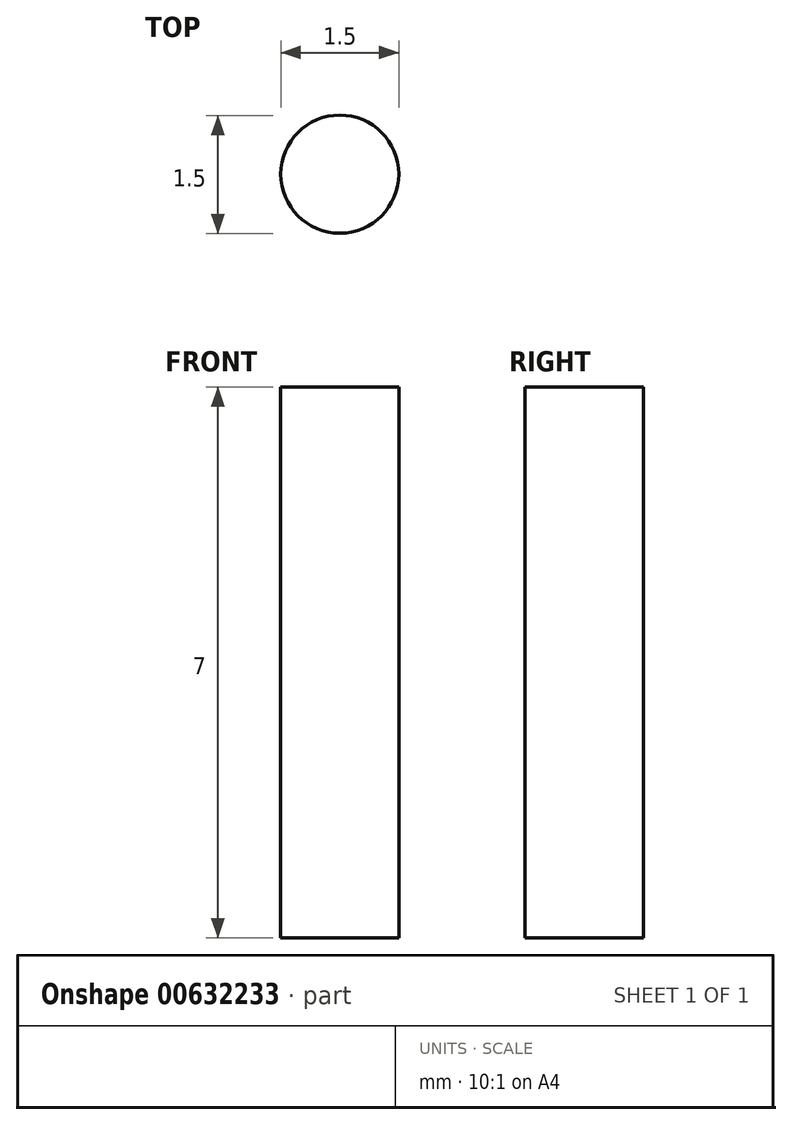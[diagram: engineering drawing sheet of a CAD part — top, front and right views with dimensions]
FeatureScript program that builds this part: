
annotation { "Feature Type Name" : "Feature", "Feature Type Description" : "" }
export const myFeature = defineFeature(function(context is Context, id is Id, definition is map)
    precondition{}
    {
        {
            var Q0;
            Q0=qCreatedBy(makeId("Top.planeOp"),FACE);
            var sketch = newSketch(context, id + "F0", { "sketchPlane" : qUnion([Q0])});
            skCircle(sketch, "E0", {"center": v(-13.28, 7.7) * mm, "radius": 0.75 * mm});
            skCircle(sketch, "E1", {"center": v(-7.79, 7.36) * mm, "radius": 1 * mm});
            skLineSegment(sketch, "E2.bottom", {"start": v(-10.46, 9.93) * mm, "end": v(-4.85, 9.93) * mm});
            skLineSegment(sketch, "E2.top", {"start": v(-10.46, 4.96) * mm, "end": v(-4.85, 4.96) * mm});
            skLineSegment(sketch, "E2.left", {"start": v(-10.46, 9.93) * mm, "end": v(-10.46, 4.96) * mm});
            skLineSegment(sketch, "E2.right", {"start": v(-4.85, 9.93) * mm, "end": v(-4.85, 4.96) * mm});
            skSolve(sketch);
        }
        {
            var Q0;
            Q0=makeQuery(id+"F0.imprint","IMPRINT",FACE,{"disambiguationData":[TD([[makeQuery(id+"F0.imprint","IMPRINT",EDGE,{"derivedFrom":sQuery(id+"F0.wireOp",EDGE,"PgbxZIXl-KwP4-Xyha-hbTg-DCnOzSjw6wvr.bottom")}),-1.0]])]});
            var Q1;
            Q1=makeQuery(id+"F0.imprint","IMPRINT",FACE,{"disambiguationData":[TD([[makeQuery(id+"F0.imprint","IMPRINT",EDGE,{"derivedFrom":sQuery(id+"F0.wireOp",EDGE,"E0")}),1.0]])]});
            extrude(context, id + "F1", {"entities" : qUnion([Q0, Q1]), "depth" : 7 * mm, "offsetDistance" : 25 * mm});
        }
    });
